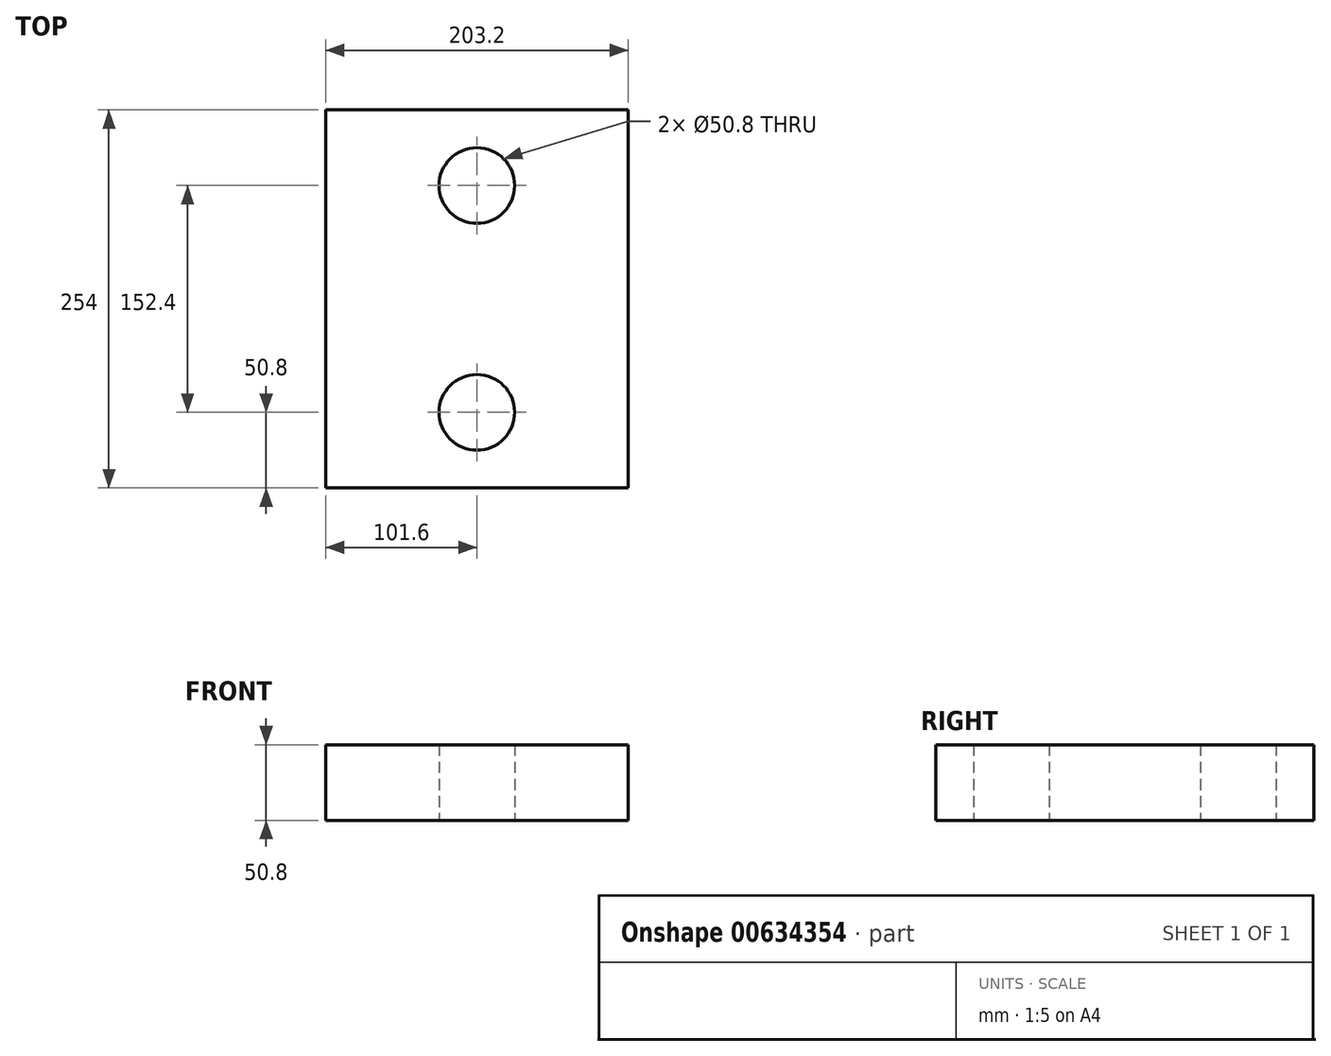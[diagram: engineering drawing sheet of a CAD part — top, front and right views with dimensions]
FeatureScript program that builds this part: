
annotation { "Feature Type Name" : "Feature", "Feature Type Description" : "" }
export const myFeature = defineFeature(function(context is Context, id is Id, definition is map)
    precondition{}
    {
        {
            var Q0;
            Q0=qCreatedBy(makeId("Top.planeOp"),FACE);
            var sketch = newSketch(context, id + "F0", { "sketchPlane" : qUnion([Q0])});
            skLineSegment(sketch, "E0.bottom", {"start": v(0, 0) * mm, "end": v(203.2, 0) * mm});
            skLineSegment(sketch, "E0.top", {"start": v(0, 254) * mm, "end": v(203.2, 254) * mm});
            skLineSegment(sketch, "E0.left", {"start": v(0, 0) * mm, "end": v(0, 254) * mm});
            skLineSegment(sketch, "E0.right", {"start": v(203.2, 0) * mm, "end": v(203.2, 254) * mm});
            skCircle(sketch, "E1", {"center": v(101.6, 203.2) * mm, "radius": 25.4 * mm});
            skPoint(sketch, "E1.centerSnap0", {"position": v(101.6, 254) * mm});
            skLineSegment(sketch, "E2", {"start": v(0, 127) * mm, "end": v(203.2, 127) * mm, "construction": true});
            skCircle(sketch, "E3.MirrorC", {"center": v(101.6, 50.8) * mm, "radius": 25.4 * mm});
            skSolve(sketch);
        }
        {
            var Q0;
            Q0=makeQuery(id+"F0.imprint","IMPRINT",FACE,{"disambiguationData":[TD([[makeQuery(id+"F0.imprint","IMPRINT",EDGE,{"derivedFrom":sQuery(id+"F0.wireOp",EDGE,"E0.bottom")}),1.0]])]});
            extrude(context, id + "F1", {"entities" : qUnion([Q0]), "depth" : 50.8 * mm, "offsetDistance" : 25.4 * mm});
        }
    });
